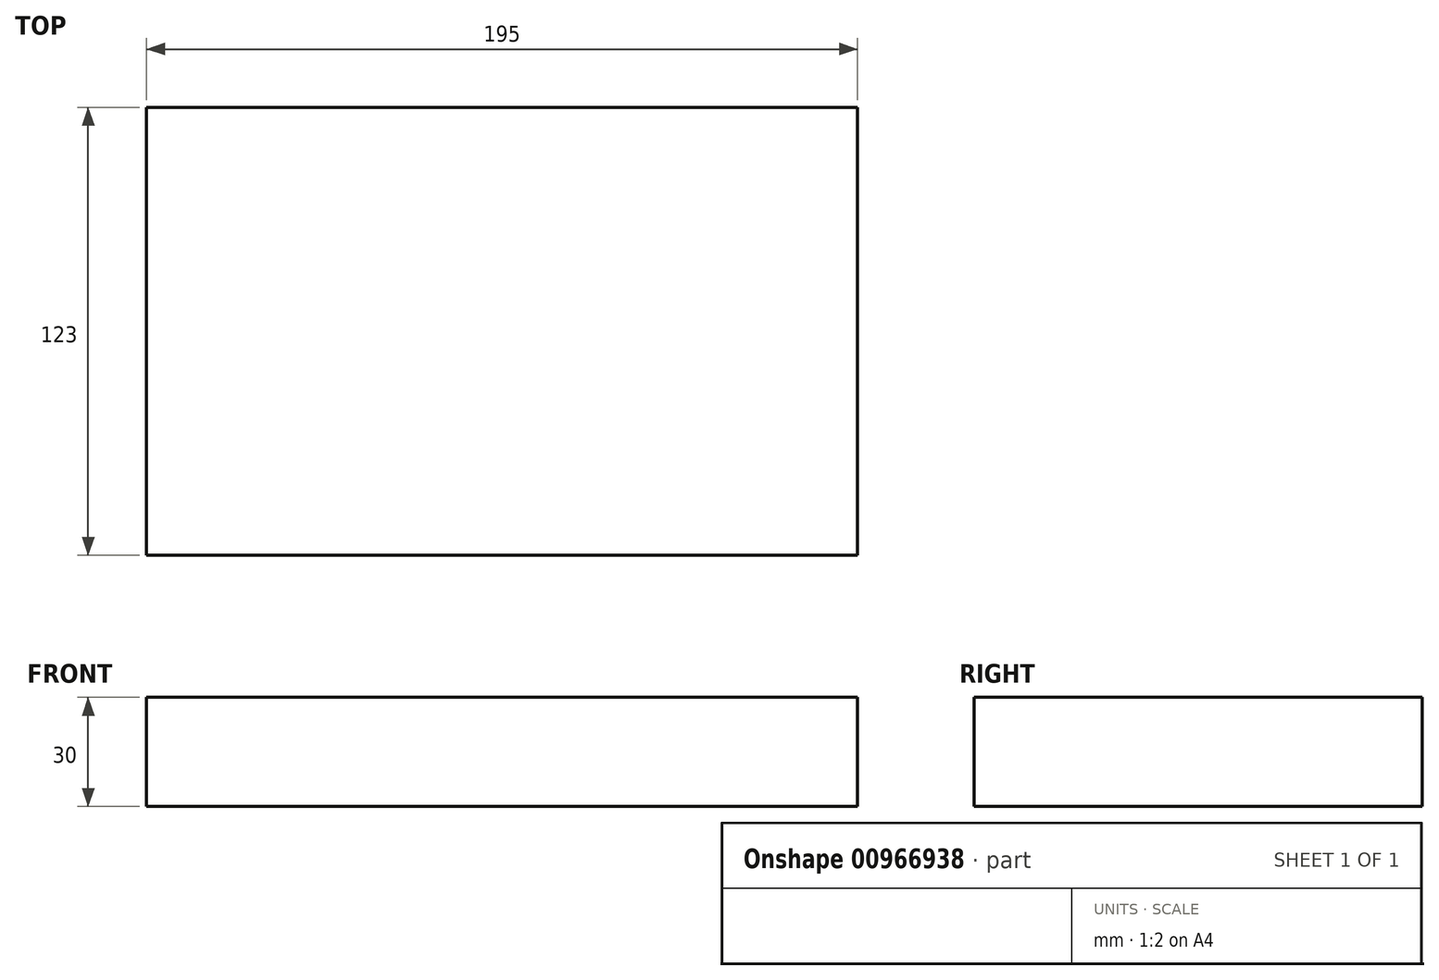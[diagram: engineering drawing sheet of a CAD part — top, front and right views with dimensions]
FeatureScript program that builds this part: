
annotation { "Feature Type Name" : "Feature", "Feature Type Description" : "" }
export const myFeature = defineFeature(function(context is Context, id is Id, definition is map)
    precondition{}
    {
        {
            var Q0;
            Q0=qCreatedBy(makeId("Top.planeOp"),FACE);
            var sketch = newSketch(context, id + "F0", { "sketchPlane" : qUnion([Q0])});
            skLineSegment(sketch, "E0.bottom", {"start": v(0, 0) * mm, "end": v(195, 0) * mm});
            skLineSegment(sketch, "E0.top", {"start": v(0, -123) * mm, "end": v(195, -123) * mm});
            skLineSegment(sketch, "E0.left", {"start": v(0, 0) * mm, "end": v(0, -123) * mm});
            skLineSegment(sketch, "E0.right", {"start": v(195, 0) * mm, "end": v(195, -123) * mm});
            skSolve(sketch);
        }
        {
            var Q0;
            Q0 = qSketchRegion(id + "F0", true);
            extrude(context, id + "F1", {"entities" : qUnion([Q0]), "depth" : 30 * mm, "offsetDistance" : 25 * mm});
        }
    });
